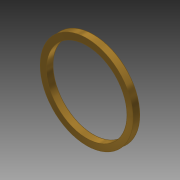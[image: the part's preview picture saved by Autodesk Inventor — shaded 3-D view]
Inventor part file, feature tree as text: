
AUTODESK INVENTOR PART (.ipt)
format: ipt  version: 2014 SP1 (Build 180222100, 222)  size: 87,040 bytes
history: native  units: in
note: dims shown in document units (in); Inventor stores cm internally (conversion verified against a paired STEP export)
features: extrude x1, sketch x1
ambient origin geometry x8: Origin, YZ Plane, XZ Plane, XY Plane, X Axis, Y Axis, Z Axis, Center Point
bodies: Solid1 (feature_tree)
feature tree (2):
  extrude  "Extrusion1"  Depth=0.3375in
  sketch  "Sketch1"  dims[d0=0.379in d2=0.437in d3=0.3375in d4=0.0in]
